# Revit family: Lighting_Outside_L-L-Luce-Light_Plin-5
name_source: partatom
category: Lighting Fixtures
units: mm (PartAtom-declared; Revit-internal decimal feet)

## family parameters
Always vertical = No
Cut with Voids When Loaded = No
Light Source = Yes
OmniClass Number = 23.80.70.00
OmniClass Title = Lighting
Part Type = Normal
Room Calculation Point = No
Round Connector Dimension = Use Diameter
Shared = No
Work Plane-Based = Yes

## types (3) — shared parameters
Color Filter = 16777215
Default Elevation = 1219 mm
Dimming Lamp Color Temperature Shift = <None>
Emit Shape Visible in Rendering = No
Emit from Circle Diameter = 25 mm  [stored 0.082021 ft]
Installation instructions = https://www.lucelight.it
Luce-Light_Applications = floor
Luce-Light_Body_material = head in aluminium, column in stainless steel
Luce-Light_Classification = CE
Luce-Light_Color_Rendering_Index_CRI = 80
Luce-Light_Finishes_material = anthracite, cor-ten, white, grey
Luce-Light_IK = 07
Luce-Light_IP = 65
Luce-Light_LED_colour = 2700K, 3000K, 4000K
Luce-Light_LED_light_sources = 1 power LED, 3-step MacAdam, 50 000h L90 B10 (Ta 25°C)
Luce-Light_Mounting = surface mounted
Luce-Light_Note = Non-standard heights available on request
Luce-Light_Optical_assembly = asymmetrical
Luce-Light_Power = 8W
Luce-Light_Power_Class = 230Vac
Luce-Light_Screen_material = serigraphed, tempered extra-clear glass
Luce-Light_Total_flow_rate = 173 lm (3000K)
Luce-Light_lumen-output-at-source = 488 lm (3000K)
Manufacturer = L&L Luce&Light
Material = Metal-Luce&Light-Stainless steel – aluminium
Nominal height = 585 mm
Nominal width = Ø125 mm
Primary material = head in aluminium, column in stainless steel
Product Guid = 9e736974-c920-4878-a1bc-51a0a79b137c
Product data url = https://www.bimobject.com
Product url = https://www.lucelight.it
Secondary material = Body in steel, head in anticorodal aluminium
Technical description = https://www.lucelight.it
Tilt Angle = 90.00°
URL = https://www.lucelight.it
Wattage Comments = 8W

## per-type parameters (varying)
| type | Photometric Web File |
| PLIN 5.1 A 4000K 8W 230Vac h585 | PLIN 5.1 A [4000K 8W 230Vac] h585.IES |
| PLIN 5.1 A 3000K 8W 230Vac h585 | PLIN 5.1 A [3000K 8W 230Vac] h585.IES |
| PLIN 5.1 A 2700K 8W 230Vac h585 | PLIN 5.1 A [2700K 8W 230Vac] h585.IES |

note: [stored X ft] marks values corroborated as IEEE doubles in the binary element streams (Revit-internal decimal feet)
